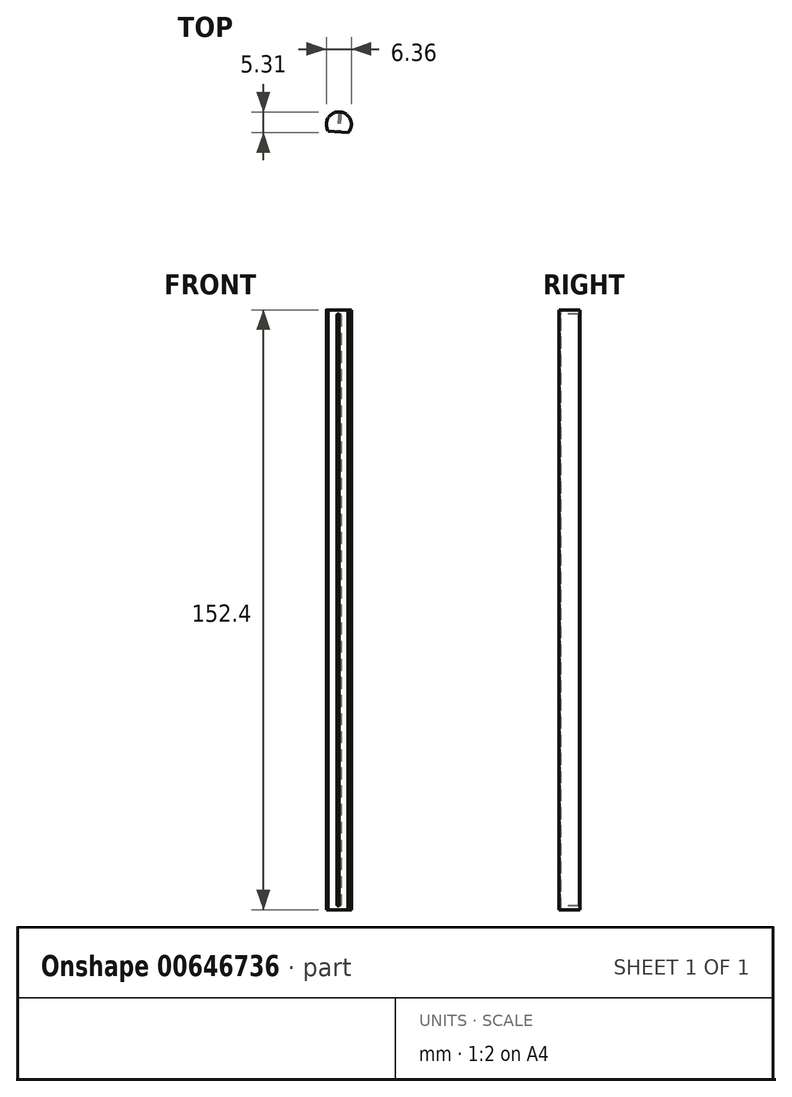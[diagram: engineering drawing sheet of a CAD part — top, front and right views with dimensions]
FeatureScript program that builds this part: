
annotation { "Feature Type Name" : "Feature", "Feature Type Description" : "" }
export const myFeature = defineFeature(function(context is Context, id is Id, definition is map)
    precondition{}
    {
        {
            var Q0;
            Q0=qCreatedBy(makeId("Top.planeOp"),FACE);
            var sketch = newSketch(context, id + "F0", { "sketchPlane" : qUnion([Q0])});
            skCircle(sketch, "E0", {"center": v(0, 0) * mm, "radius": 3.18 * mm});
            skSolve(sketch);
        }
        {
            var Q0;
            Q0=makeQuery(id+"F0.imprint","IMPRINT",FACE,{"disambiguationData":[TD([[makeQuery(id+"F0.imprint","IMPRINT",EDGE,{"derivedFrom":sQuery(id+"F0.wireOp",EDGE,"E0")}),1.0]])]});
            extrude(context, id + "F1", {"entities" : qUnion([Q0]), "endBound" : BoundingType.SYMMETRIC, "depth" : 152.4 * mm, "offsetDistance" : 25.4 * mm});
        }
        {
            var Q0;
            Q0=makeQuery(id+"F1.opExtrude","CAP_FACE",FACE,{"disambiguationData":[OSD([sQuery(id+"F0.wireOp",EDGE,"E0")])],"isStart":false});
            var sketch = newSketch(context, id + "F2", { "sketchPlane" : qUnion([Q0])});
            skLineSegment(sketch, "E1", {"start": v(-2.7, -1.66) * mm, "end": v(2.35, -2.13) * mm});
            skSolve(sketch);
        }
        {
            var Q0;
            {var subQ0=sQuery(id+"F2.wireOp",EDGE,"E1");Q0=makeQuery(id+"F2.imprint","IMPRINT",FACE,{"disambiguationData":[TD([[makeQuery(id+"F2.imprint","IMPRINT",EDGE,{"derivedFrom":subQ0}),-1.0]])]});}
            extrude(context, id + "F3", {"entities" : qUnion([Q0]), "operationType" : NewBodyOperationType.REMOVE, "oppositeDirection" : true, "depth" : 152.4 * mm, "offsetDistance" : 25.4 * mm});
        }
        {
            var Q0;
            Q0=makeQuery(id+"F3.boolean.opBoolean","COPY",FACE,{"derivedFrom":makeQuery(id+"F3.opExtrude","SWEPT_FACE",FACE,{"disambiguationData":[OSD([sQuery(id+"F2.wireOp",EDGE,"E1")])]})});
            var sketch = newSketch(context, id + "F4", { "sketchPlane" : qUnion([Q0])});
            skPoint(sketch, "E2", {"position": v(-0.25, 74.93) * mm});
            skPoint(sketch, "E3", {"position": v(0.25, 74.93) * mm});
            skLineSegment(sketch, "E4", {"start": v(-0.25, 74.93) * mm, "end": v(0.25, 74.93) * mm});
            skLineSegment(sketch, "E5.MirrorCS", {"start": v(-0.25, -74.93) * mm, "end": v(0.25, -74.93) * mm});
            skLineSegment(sketch, "E6", {"start": v(-0.25, -74.93) * mm, "end": v(-0.25, 74.93) * mm});
            skLineSegment(sketch, "E7", {"start": v(0.25, 74.93) * mm, "end": v(0.25, -74.93) * mm});
            skArc(sketch, "E8", {"start": v(-0.25, -74.93) * mm, "mid": v(0, -75.18) * mm, "end": v(0.25, -74.93) * mm});
            skArc(sketch, "E9", {"start": v(-0.25, 74.93) * mm, "mid": v(0, 75.18) * mm, "end": v(0.25, 74.93) * mm});
            skSolve(sketch);
        }
        {
            var Q0;
            Q0=makeQuery(id+"F4.imprint","IMPRINT",FACE,{"disambiguationData":[TD([[makeQuery(id+"F4.imprint","IMPRINT",EDGE,{"derivedFrom":sQuery(id+"F4.wireOp",EDGE,"E4")}),-1.0]])]});
            var Q1;
            Q1=makeQuery(id+"F4.imprint","IMPRINT",FACE,{"disambiguationData":[TD([[makeQuery(id+"F4.imprint","IMPRINT",EDGE,{"derivedFrom":sQuery(id+"F4.wireOp",EDGE,"E5.MirrorCS")}),-1.0]])]});
            var Q2;
            Q2=makeQuery(id+"F4.imprint","IMPRINT",FACE,{"disambiguationData":[TD([[makeQuery(id+"F4.imprint","IMPRINT",EDGE,{"derivedFrom":sQuery(id+"F4.wireOp",EDGE,"E4")}),1.0]])]});
            extrude(context, id + "F5", {"entities" : qUnion([Q0, Q1, Q2]), "operationType" : NewBodyOperationType.REMOVE, "oppositeDirection" : true, "depth" : 25.4 * mm, "offsetDistance" : 25.4 * mm});
        }
    });
